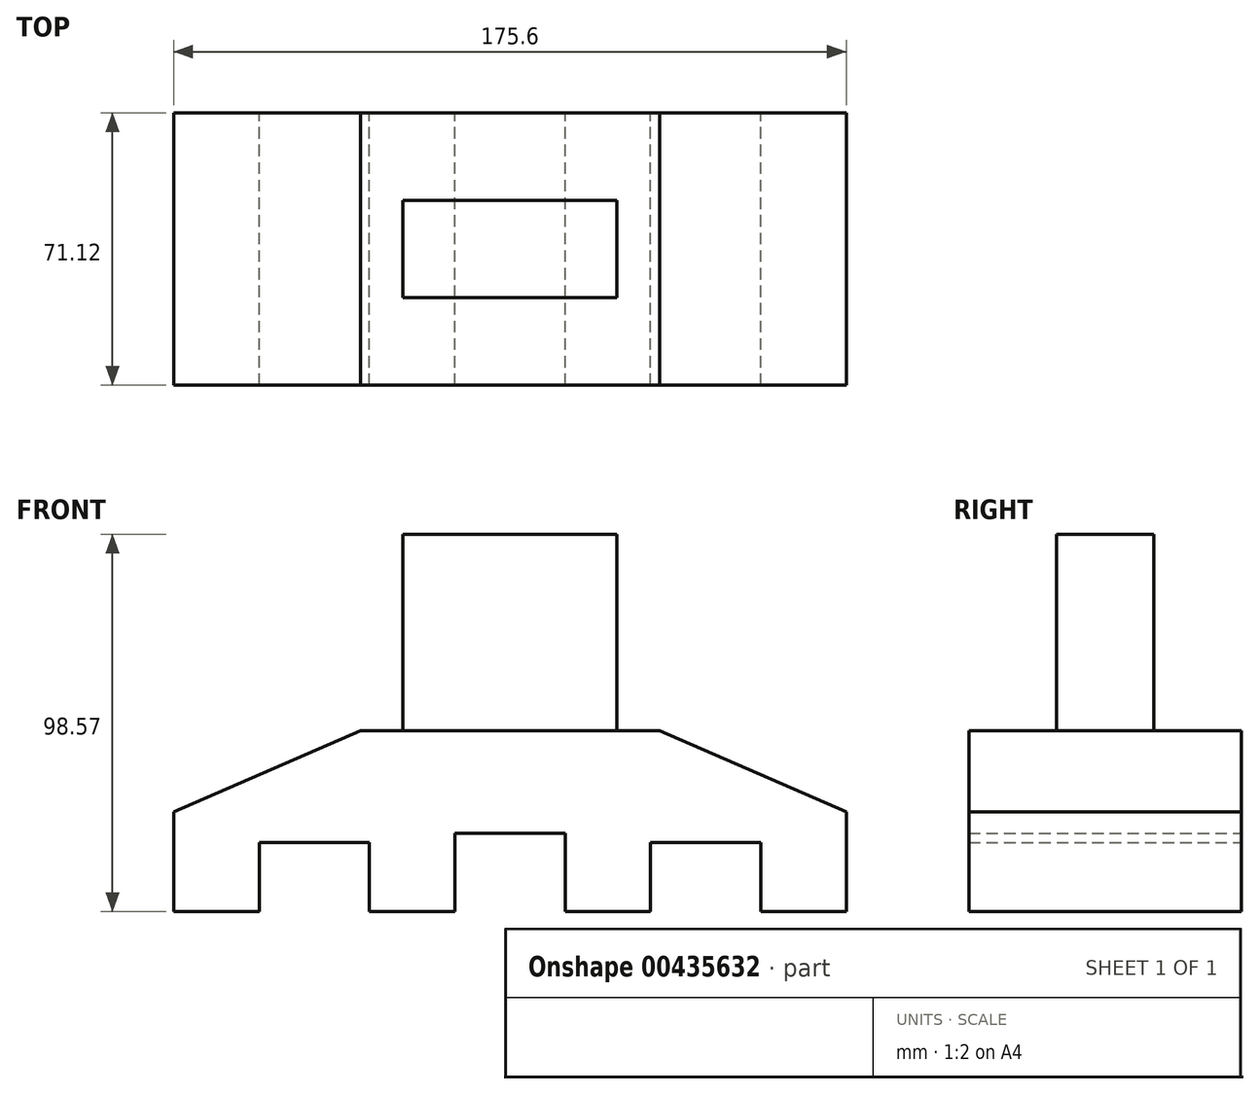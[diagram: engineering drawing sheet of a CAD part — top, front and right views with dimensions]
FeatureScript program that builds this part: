
annotation { "Feature Type Name" : "Feature", "Feature Type Description" : "" }
export const myFeature = defineFeature(function(context is Context, id is Id, definition is map)
    precondition{}
    {
        {
            var Q0;
            Q0=qCreatedBy(makeId("Front.planeOp"),FACE);
            var sketch = newSketch(context, id + "F0", { "sketchPlane" : qUnion([Q0])});
            skLineSegment(sketch, "E0", {"start": v(0, 0) * mm, "end": v(0, 133.52) * mm, "construction": true});
            skLineSegment(sketch, "E1", {"start": v(0, 0) * mm, "end": v(-60.17, 0) * mm, "construction": true});
            skLineSegment(sketch, "E2", {"start": v(-65.47, 12.35) * mm, "end": v(-87.8, 12.35) * mm});
            skLineSegment(sketch, "E3", {"start": v(-87.8, 12.35) * mm, "end": v(-87.8, 38.37) * mm});
            skLineSegment(sketch, "E4", {"start": v(-87.8, 38.37) * mm, "end": v(-39.07, 59.6) * mm});
            skLineSegment(sketch, "E5", {"start": v(-39.07, 59.6) * mm, "end": v(0, 59.6) * mm});
            skLineSegment(sketch, "E6", {"start": v(-65.47, 12.35) * mm, "end": v(-65.47, 30.37) * mm});
            skLineSegment(sketch, "E7", {"start": v(-65.47, 30.37) * mm, "end": v(-36.7, 30.37) * mm});
            skLineSegment(sketch, "E8", {"start": v(-36.7, 30.37) * mm, "end": v(-36.7, 12.35) * mm});
            skLineSegment(sketch, "E9", {"start": v(-36.7, 12.35) * mm, "end": v(-14.38, 12.35) * mm});
            skLineSegment(sketch, "E10", {"start": v(-14.38, 12.35) * mm, "end": v(-14.38, 32.8) * mm});
            skLineSegment(sketch, "E11.MirrorCS", {"start": v(14.38, 12.35) * mm, "end": v(14.38, 32.8) * mm});
            skLineSegment(sketch, "E12.MirrorCS", {"start": v(36.7, 12.35) * mm, "end": v(14.38, 12.35) * mm});
            skLineSegment(sketch, "E13.MirrorCS", {"start": v(65.47, 12.35) * mm, "end": v(87.8, 12.35) * mm});
            skLineSegment(sketch, "E14.MirrorCS", {"start": v(65.47, 12.35) * mm, "end": v(65.47, 30.37) * mm});
            skLineSegment(sketch, "E15.MirrorCS", {"start": v(65.47, 30.37) * mm, "end": v(36.7, 30.37) * mm});
            skLineSegment(sketch, "E16.MirrorCS", {"start": v(87.8, 12.35) * mm, "end": v(87.8, 38.37) * mm});
            skLineSegment(sketch, "E17.MirrorCS", {"start": v(39.07, 59.6) * mm, "end": v(0, 59.6) * mm});
            skLineSegment(sketch, "E18.MirrorCS", {"start": v(87.8, 38.37) * mm, "end": v(39.07, 59.6) * mm});
            skLineSegment(sketch, "E19.MirrorCS", {"start": v(36.7, 30.37) * mm, "end": v(36.7, 12.35) * mm});
            skLineSegment(sketch, "E20", {"start": v(-14.38, 32.8) * mm, "end": v(14.38, 32.8) * mm});
            skSolve(sketch);
        }
        {
            var Q0;
            Q0=makeQuery(id+"F0.imprint","IMPRINT",FACE,{"disambiguationData":[TD([[makeQuery(id+"F0.imprint","IMPRINT",EDGE,{"derivedFrom":sQuery(id+"F0.wireOp",EDGE,"E2")}),-1.0]])]});
            extrude(context, id + "F1", {"entities" : qUnion([Q0]), "endBound" : BoundingType.SYMMETRIC, "depth" : 71.12 * mm});
        }
        {
            var Q0;
            Q0=qCreatedBy(makeId("Front.planeOp"),FACE);
            var sketch = newSketch(context, id + "F2", { "sketchPlane" : qUnion([Q0])});
            skLineSegment(sketch, "E21.bottom", {"start": v(-27.94, 59.6) * mm, "end": v(27.94, 59.6) * mm});
            skLineSegment(sketch, "E21.top", {"start": v(-27.94, 110.92) * mm, "end": v(27.94, 110.92) * mm});
            skLineSegment(sketch, "E21.left", {"start": v(-27.94, 59.6) * mm, "end": v(-27.94, 110.92) * mm});
            skLineSegment(sketch, "E22", {"start": v(0, 0) * mm, "end": v(0, 120.74) * mm, "construction": true});
            skLineSegment(sketch, "E23.MirrorCS", {"start": v(27.94, 59.6) * mm, "end": v(27.94, 110.92) * mm});
            skSolve(sketch);
        }
        {
            var Q0;
            Q0 = qSketchRegion(id + "F2", true);
            extrude(context, id + "F3", {"entities" : qUnion([Q0]), "endBound" : BoundingType.SYMMETRIC, "depth" : 25.4 * mm});
        }
    });
